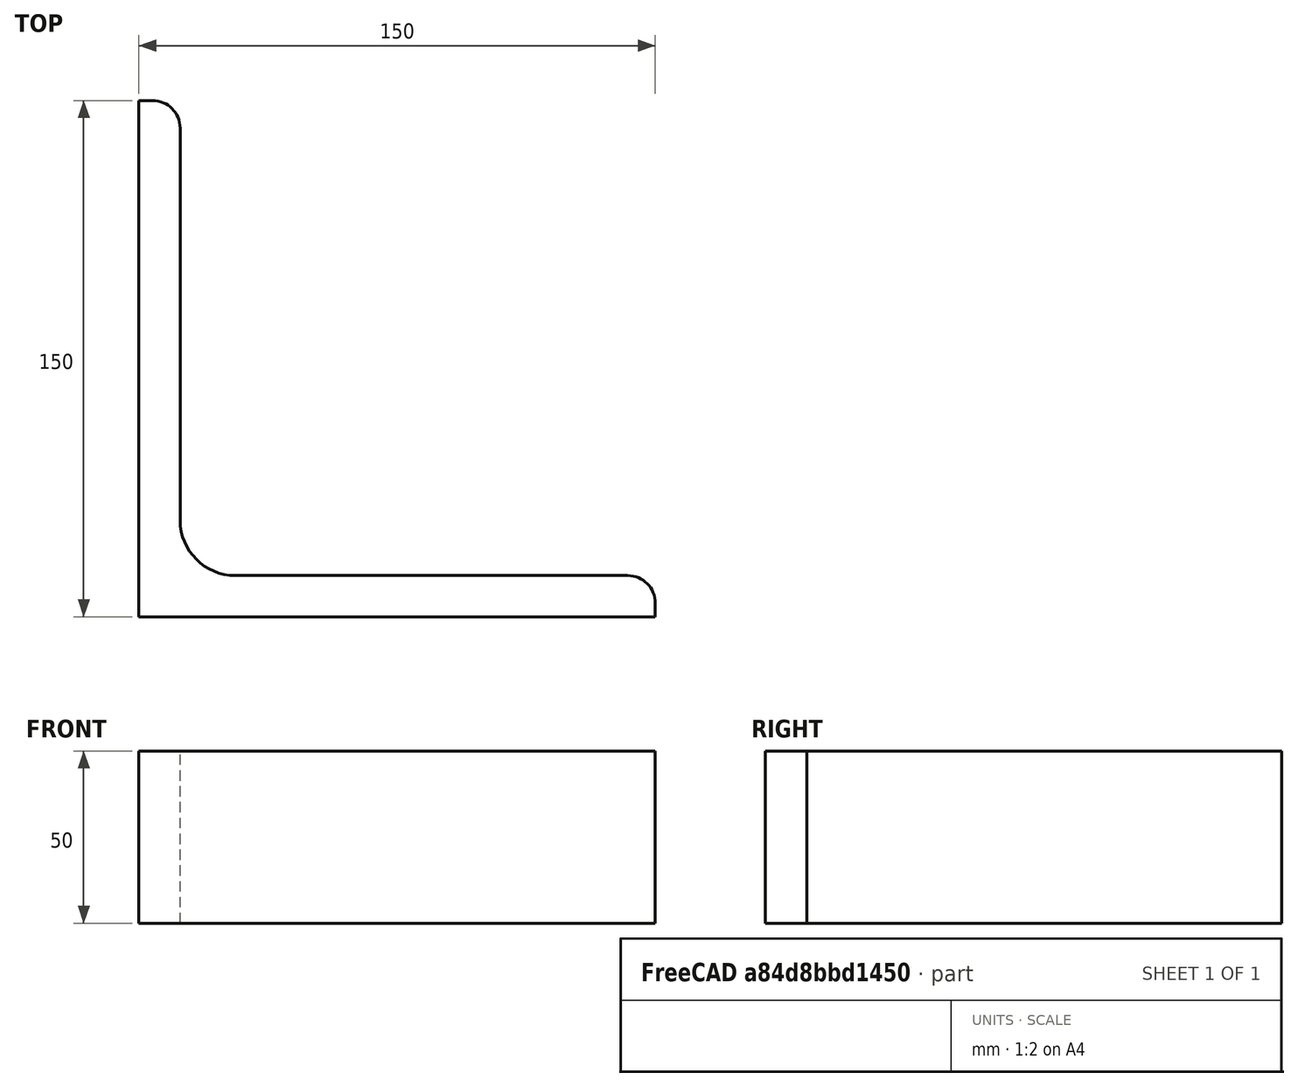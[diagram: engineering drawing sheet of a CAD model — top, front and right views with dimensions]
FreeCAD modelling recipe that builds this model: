
FCSTD DOCUMENT  (FreeCAD 0.15R4671 (Git))
Label: Angle Bar L150x150x12 EN10056 S235JR
License: All rights reserved
LicenseURL: http://en.wikipedia.org/wiki/All_rights_reserved
objects: Sketcher::SketchObject×1, Part::Extrusion×1
note: 2 computed .brp shape members not serialized (recipe doc carries the construction recipe); baked Part::Feature solids carry a one-line shape summary decoded from their .brp

FEATURE [Sketcher::SketchObject] Sketch
  sketch-geometry (9):
    g0: LineSegment StartX=0 StartY=0 StartZ=0 EndX=150 EndY=0 EndZ=0
    g1: LineSegment StartX=150 StartY=0 StartZ=0 EndX=150 EndY=4 EndZ=0
    g2: LineSegment StartX=142 StartY=12 StartZ=0 EndX=28 EndY=12 EndZ=0
    g3: LineSegment StartX=0 StartY=0 StartZ=0 EndX=0 EndY=150 EndZ=0
    g4: LineSegment StartX=0 StartY=150 StartZ=0 EndX=4 EndY=150 EndZ=0
    g5: LineSegment StartX=12 StartY=142 StartZ=0 EndX=12 EndY=28 EndZ=0
    g6: ArcOfCircle CenterX=28 CenterY=28 CenterZ=0 NormalX=0 NormalY=0 NormalZ=1 Radius=16 StartAngle=3.14159 EndAngle=4.71239
    g7: ArcOfCircle CenterX=4 CenterY=142 CenterZ=0 NormalX=0 NormalY=0 NormalZ=1 Radius=8 StartAngle=0 EndAngle=1.5708
    g8: ArcOfCircle CenterX=142 CenterY=4 CenterZ=0 NormalX=0 NormalY=0 NormalZ=1 Radius=8 StartAngle=0 EndAngle=1.5708
  constraints (23):
    c: Coincident(g0,g-1)
    c: Horizontal(g0)
    c: Coincident(g1,g0)
    c: Vertical(g1)
    c: Horizontal(g2)
    c: Coincident(g3,g-1)
    c: Vertical(g3)
    c: Coincident(g4,g3)
    c: Horizontal(g4)
    c: Vertical(g5)
    c: Tangent(g5,g6) = -1.5708
    c: Tangent(g2,g6) = 1.5708
    c: Tangent(g4,g7) = 1.5708
    c: Tangent(g5,g7) = 1.5708
    c: Tangent(g2,g8) = -1.5708
    c: Tangent(g1,g8) = -1.5708
    c: DistanceX(g0) = 150
    c: DistanceY(g3) = 150
    c: DistanceY(g0,g2) = 12
    c: DistanceX(g3,g5) = 12
    c: Radius(g6) = 16
    c: Radius(g8) = 8
    c: Radius(g7) = 8
FEATURE [Part::Extrusion] Extrude  label="Angle Bar L150x150x12 EN10056 S235JR"
  Base = -> Sketch
  Dir = (0,0,50)
  Solid = true
